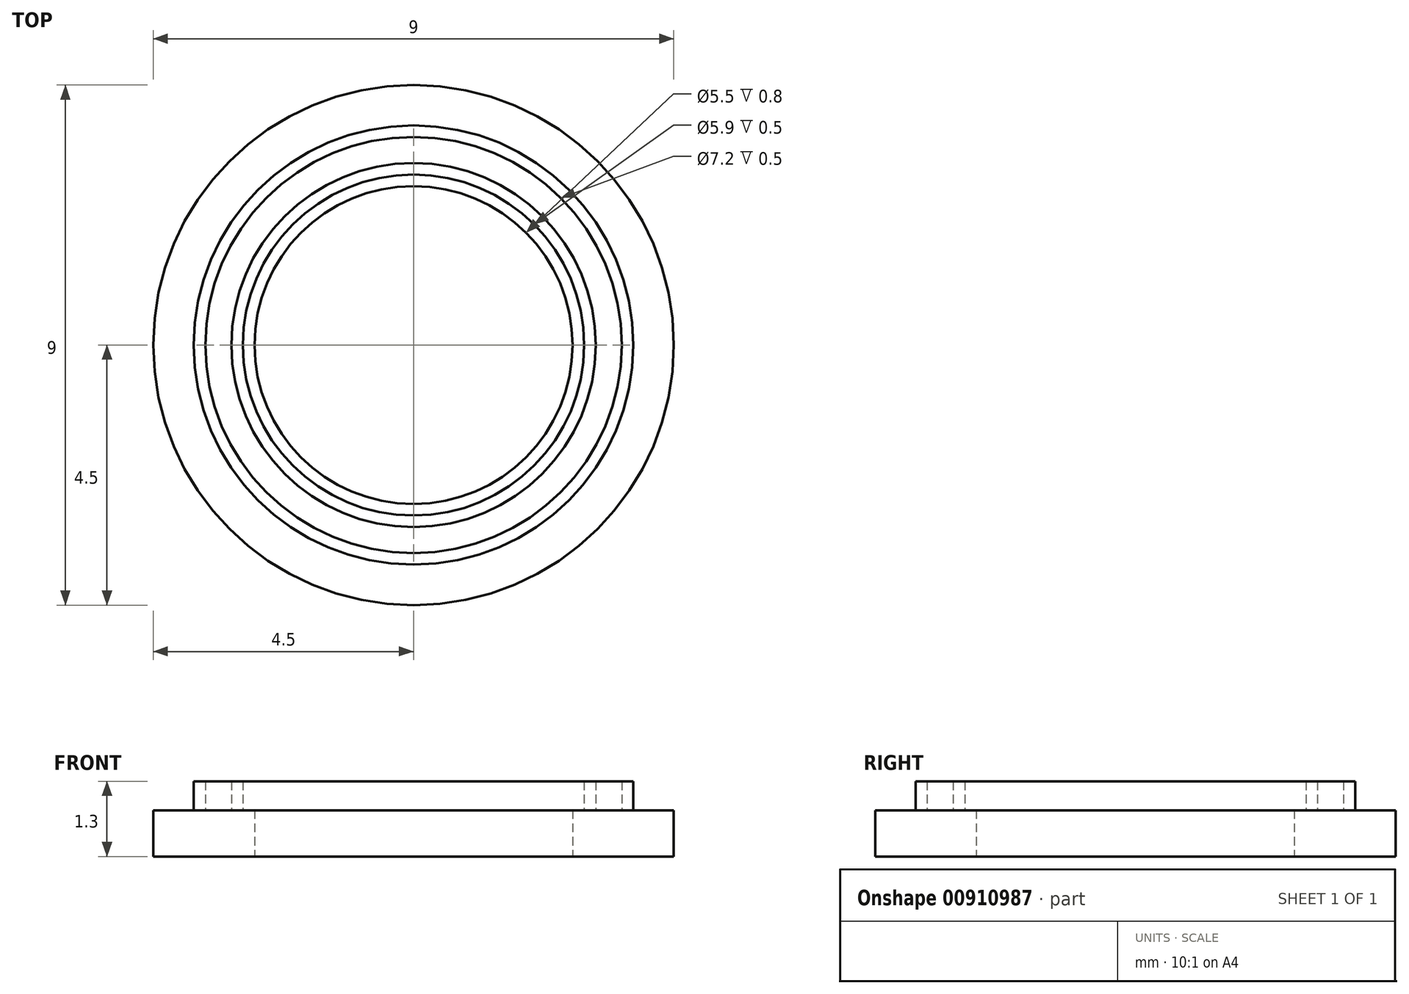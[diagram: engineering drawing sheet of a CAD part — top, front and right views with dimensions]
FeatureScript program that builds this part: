
annotation { "Feature Type Name" : "Feature", "Feature Type Description" : "" }
export const myFeature = defineFeature(function(context is Context, id is Id, definition is map)
    precondition{}
    {
        {
            var Q0;
            Q0=qCreatedBy(makeId("Top.planeOp"),FACE);
            var sketch = newSketch(context, id + "F0", { "sketchPlane" : qUnion([Q0])});
            skCircle(sketch, "E0", {"center": v(0, 0) * mm, "radius": 4.5 * mm});
            skCircle(sketch, "E1", {"center": v(0, 0) * mm, "radius": 2.75 * mm});
            skSolve(sketch);
        }
        {
            var Q0;
            Q0 = qSketchRegion(id + "F0", true);
            extrude(context, id + "F1", {"entities" : qUnion([Q0]), "depth" : 0.8 * mm, "offsetDistance" : 25 * mm});
        }
        {
            var Q0;
            Q0=makeQuery(id+"F1.opExtrude","CAP_FACE",FACE,{"disambiguationData":[OSD([sQuery(id+"F0.wireOp",EDGE,"E0"),sQuery(id+"F0.wireOp",EDGE,"E1")])],"isStart":false});
            var sketch = newSketch(context, id + "F2", { "sketchPlane" : qUnion([Q0])});
            skCircle(sketch, "E2", {"center": v(0, 0) * mm, "radius": 3.15 * mm});
            skCircle(sketch, "E3", {"center": v(0, 0) * mm, "radius": 2.95 * mm});
            skSolve(sketch);
        }
        {
            var Q0;
            Q0 = qSketchRegion(id + "F2", true);
            extrude(context, id + "F3", {"entities" : qUnion([Q0]), "operationType" : NewBodyOperationType.ADD, "depth" : 0.5 * mm, "offsetDistance" : 25 * mm});
        }
        {
            var Q0;
            {var subQ0=sQuery(id+"F0.wireOp",EDGE,"E0");Q0=makeQuery(id+"F3.boolean.opBoolean","SPLIT",FACE,{"disambiguationData":[TD([makeQuery(id+"F1.opExtrude","SWEPT_FACE",FACE,{"disambiguationData":[OSD([subQ0])]})])],"derivedFrom":makeQuery(id+"F1.opExtrude","CAP_FACE",FACE,{"disambiguationData":[OSD([subQ0,sQuery(id+"F0.wireOp",EDGE,"E1")])],"isStart":false})});}
            var sketch = newSketch(context, id + "F4", { "sketchPlane" : qUnion([Q0])});
            skCircle(sketch, "E4", {"center": v(0, 0) * mm, "radius": 3.8 * mm});
            skCircle(sketch, "E5", {"center": v(0, 0) * mm, "radius": 3.6 * mm});
            skSolve(sketch);
        }
        {
            var Q0;
            Q0 = qSketchRegion(id + "F4", true);
            extrude(context, id + "F5", {"entities" : qUnion([Q0]), "operationType" : NewBodyOperationType.ADD, "depth" : 0.5 * mm, "offsetDistance" : 25 * mm});
        }
    });
